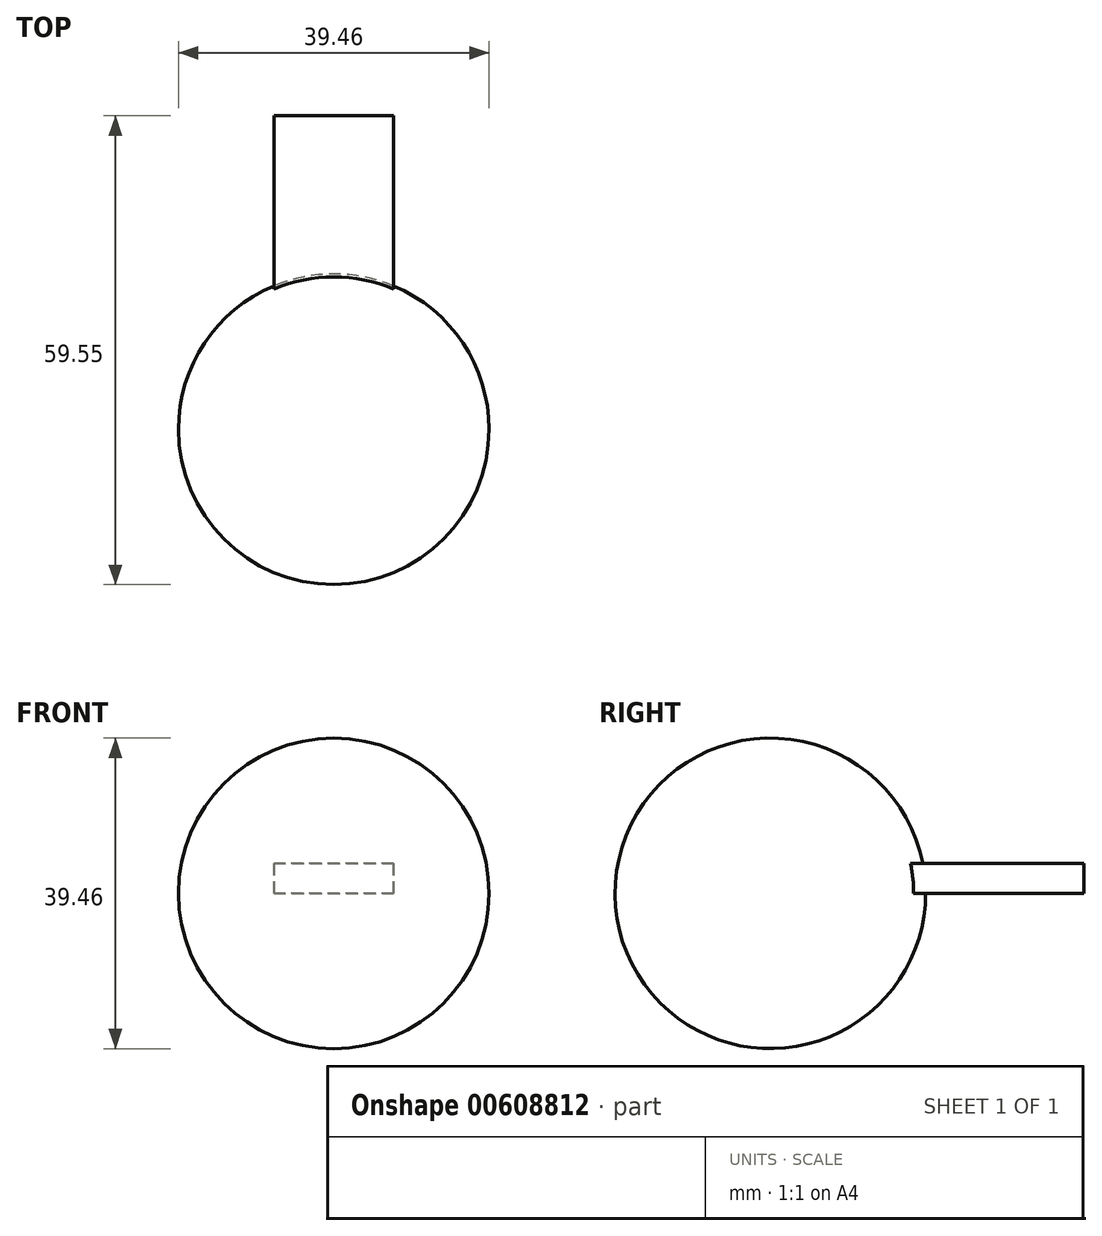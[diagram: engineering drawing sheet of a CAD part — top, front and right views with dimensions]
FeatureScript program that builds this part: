
annotation { "Feature Type Name" : "Feature", "Feature Type Description" : "" }
export const myFeature = defineFeature(function(context is Context, id is Id, definition is map)
    precondition{}
    {
        {
            var Q0;
            Q0=qCreatedBy(makeId("Front.planeOp"),FACE);
            var sketch = newSketch(context, id + "F0", { "sketchPlane" : qUnion([Q0])});
            skCircle(sketch, "E0", {"center": v(0, 0) * mm, "radius": 19.73 * mm});
            skLineSegment(sketch, "E1", {"start": v(19.73, 0) * mm, "end": v(-19.73, 0) * mm});
            skSolve(sketch);
        }
        {
            var Q0;
            {var subQ0=sQuery(id+"F0.wireOp",EDGE,"E1");Q0=makeQuery(id+"F0.imprint","IMPRINT",FACE,{"disambiguationData":[TD([[makeQuery(id+"F0.imprint","IMPRINT",EDGE,{"derivedFrom":subQ0}),1.0]])]});}
            var Q1;
            Q1=sQuery(id+"F0.wireOp",EDGE,"E1");
            revolve(context, id + "F1", {"entities" : qUnion([Q0]), "axis" : qUnion([Q1]), "revolveType" : RevolveType.FULL});
        }
        {
            var Q0;
            Q0=qCreatedBy(makeId("Top.planeOp"),FACE);
            var sketch = newSketch(context, id + "F2", { "sketchPlane" : qUnion([Q0])});
            skLineSegment(sketch, "E2", {"start": v(-7.6, 19) * mm, "end": v(-7.6, 39.82) * mm});
            skLineSegment(sketch, "E3", {"start": v(-7.6, 39.82) * mm, "end": v(7.6, 39.82) * mm});
            skLineSegment(sketch, "E4", {"start": v(7.6, 39.82) * mm, "end": v(7.6, 19.24) * mm});
            skArc(sketch, "E5", {"start": v(7.6, 19.24) * mm, "mid": v(0, 19.48) * mm, "end": v(-7.6, 19) * mm});
            skSolve(sketch);
        }
        {
            var Q0;
            Q0 = qSketchRegion(id + "F2", true);
            extrude(context, id + "F3", {"entities" : qUnion([Q0]), "operationType" : NewBodyOperationType.ADD, "depth" : 3.8 * mm, "offsetDistance" : 25.4 * mm});
        }
        {
            var Q0;
            Q0=makeQuery(id+"F3.opExtrude","SWEPT_FACE",FACE,{"disambiguationData":[OSD([sQuery(id+"F2.wireOp",EDGE,"E3")])]});
            var sketch = newSketch(context, id + "F4", { "sketchPlane" : qUnion([Q0])});
            skLineSegment(sketch, "E6.bottom", {"start": v(-7.6, 3.81) * mm, "end": v(7.6, 3.81) * mm});
            skLineSegment(sketch, "E6.top", {"start": v(-7.6, 0) * mm, "end": v(7.6, 0) * mm});
            skLineSegment(sketch, "E6.left", {"start": v(-7.6, 3.81) * mm, "end": v(-7.6, 0) * mm});
            skLineSegment(sketch, "E6.right", {"start": v(7.6, 3.81) * mm, "end": v(7.6, 0) * mm});
            skSolve(sketch);
        }
        {
            var Q0;
            Q0=makeQuery(id+"F4.imprint","IMPRINT",FACE,{"disambiguationData":[TD([[makeQuery(id+"F4.imprint","IMPRINT",EDGE,{"derivedFrom":sQuery(id+"F4.wireOp",EDGE,"E6.bottom")}),1.0]])]});
            extrude(context, id + "F5", {"entities" : qUnion([Q0]), "operationType" : NewBodyOperationType.ADD, "oppositeDirection" : true, "depth" : 50.8 * mm, "offsetDistance" : 25.4 * mm});
        }
    });
